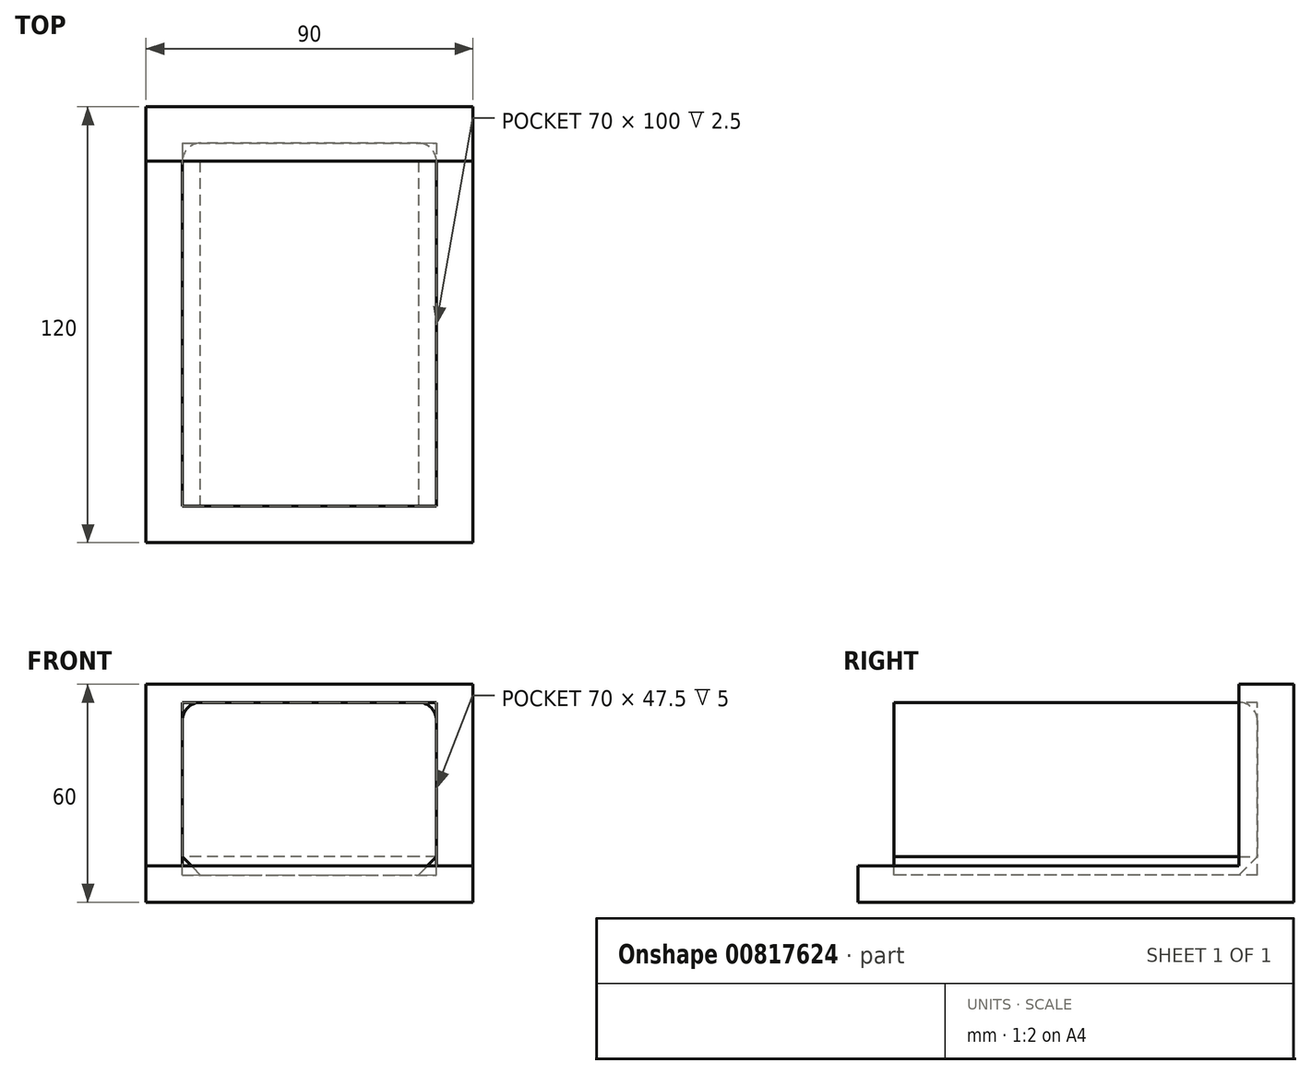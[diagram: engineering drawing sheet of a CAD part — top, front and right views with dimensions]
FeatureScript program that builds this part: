
annotation { "Feature Type Name" : "Feature", "Feature Type Description" : "" }
export const myFeature = defineFeature(function(context is Context, id is Id, definition is map)
    precondition{}
    {
        {
            var Q0;
            Q0=qCreatedBy(makeId("Top.planeOp"),FACE);
            var sketch = newSketch(context, id + "F0", { "sketchPlane" : qUnion([Q0])});
            skLineSegment(sketch, "E0.bottom", {"start": v(0, 0) * mm, "end": v(90, 0) * mm});
            skLineSegment(sketch, "E0.top", {"start": v(0, 120) * mm, "end": v(90, 120) * mm});
            skLineSegment(sketch, "E0.left", {"start": v(0, 0) * mm, "end": v(0, 120) * mm});
            skLineSegment(sketch, "E0.right", {"start": v(90, 0) * mm, "end": v(90, 120) * mm});
            skSolve(sketch);
        }
        {
            var Q0;
            Q0=qSketchRegion(id+"F0",true);
            extrude(context, id + "F1", {"entities" : qUnion([Q0]), "depth" : 10 * mm, "offsetDistance" : 25 * mm});
        }
        {
            var Q0;
            Q0=makeQuery(id+"F1.opExtrude","CAP_FACE",FACE,{"disambiguationData":[OSD([sQuery(id+"F0.wireOp",EDGE,"E0.bottom"),sQuery(id+"F0.wireOp",EDGE,"E0.top"),sQuery(id+"F0.wireOp",EDGE,"E0.left"),sQuery(id+"F0.wireOp",EDGE,"E0.right")])],"isStart":false});
            var sketch = newSketch(context, id + "F2", { "sketchPlane" : qUnion([Q0])});
            skLineSegment(sketch, "E1", {"start": v(0, 105) * mm, "end": v(90, 105) * mm});
            skSolve(sketch);
        }
        {
            var Q0;
            {var subQ0=sQuery(id+"F2.wireOp",EDGE,"E1");Q0=makeQuery(id+"F2.imprint","IMPRINT",FACE,{"disambiguationData":[TD([[makeQuery(id+"F2.imprint","IMPRINT",EDGE,{"derivedFrom":subQ0}),1.0]])]});}
            extrude(context, id + "F3", {"entities" : qUnion([Q0]), "operationType" : NewBodyOperationType.ADD, "depth" : 50 * mm, "offsetDistance" : 25 * mm});
        }
        {
            var Q0;
            Q0=makeQuery(id+"F3.opExtrude","CAP_FACE",FACE,{"disambiguationData":[OSD([sQuery(id+"F0.wireOp",EDGE,"E0.top"),sQuery(id+"F0.wireOp",EDGE,"E0.left"),sQuery(id+"F0.wireOp",EDGE,"E0.right"),sQuery(id+"F2.wireOp",EDGE,"E1")])],"isStart":false});
            cPlane(context, id + "F4", {"entities" : qUnion([Q0]), "cplaneType" : CPlaneType.OFFSET, "offset" : 5 * mm, "oppositeDirection" : true, "width" : 150 * mm, "height" : 150 * mm});
        }
        {
            var Q0;
            Q0=qCreatedBy(id+"F4.planeOp",FACE);
            var sketch = newSketch(context, id + "F5", { "sketchPlane" : qUnion([Q0])});
            skLineSegment(sketch, "E2.bottom", {"start": v(10, 110) * mm, "end": v(80, 110) * mm});
            skLineSegment(sketch, "E2.top", {"start": v(10, 10) * mm, "end": v(80, 10) * mm});
            skLineSegment(sketch, "E2.left", {"start": v(10, 110) * mm, "end": v(10, 10) * mm});
            skLineSegment(sketch, "E2.right", {"start": v(80, 110) * mm, "end": v(80, 10) * mm});
            skSolve(sketch);
        }
        {
            var Q0;
            {var subQ0=sQuery(id+"F5.wireOp",EDGE,"E2.top");Q0=makeQuery(id+"F5.imprint","IMPRINT",FACE,{"disambiguationData":[TD([[makeQuery(id+"F5.imprint","IMPRINT",EDGE,{"derivedFrom":subQ0}),1.0]])]});}
            var Q1;
            {var subQ0=sQuery(id+"F5.wireOp",EDGE,"E2.bottom");Q1=makeQuery(id+"F5.imprint","IMPRINT",FACE,{"disambiguationData":[TD([[makeQuery(id+"F5.imprint","IMPRINT",EDGE,{"derivedFrom":subQ0}),-1.0]])]});}
            extrude(context, id + "F6", {"entities" : qUnion([Q0, Q1]), "operationType" : NewBodyOperationType.REMOVE, "oppositeDirection" : true, "depth" : 47.5 * mm, "offsetDistance" : 25 * mm});
        }
        {
            var Q0;
            Q0=makeQuery(id+"F6.boolean.opBoolean","COPY",FACE,{"derivedFrom":makeQuery(id+"F6.opExtrude","CAP_FACE",FACE,{"disambiguationData":[OSD([sQuery(id+"F5.wireOp",EDGE,"E2.bottom"),sQuery(id+"F5.wireOp",EDGE,"E2.top"),sQuery(id+"F5.wireOp",EDGE,"E2.left"),sQuery(id+"F5.wireOp",EDGE,"E2.right")])],"isStart":false})});
            var Q1;
            Q1=makeQuery(id+"F6.boolean.opBoolean","COPY",FACE,{"derivedFrom":makeQuery(id+"F6.opExtrude","CAP_FACE",FACE,{"disambiguationData":[OSD([sQuery(id+"F5.wireOp",EDGE,"E2.bottom"),sQuery(id+"F5.wireOp",EDGE,"E2.top"),sQuery(id+"F5.wireOp",EDGE,"E2.left"),sQuery(id+"F5.wireOp",EDGE,"E2.right")])],"isStart":true})});
            extrude(context, id + "F7", {"entities" : qUnion([Q0]), "endBound" : BoundingType.UP_TO_SURFACE, "depth" : 40.5 * mm, "endBoundEntityFace" : qUnion([Q1]), "offsetDistance" : 25 * mm});
        }
        {
            var Q0;
            Q0=makeQuery(id+"F7.opExtrude","CAP_EDGE",EDGE,{"disambiguationData":[OSD([sQuery(id+"F5.wireOp",EDGE,"E2.right")])],"isStart":false});
            var Q1;
            Q1=makeQuery(id+"F7.opExtrude","CAP_EDGE",EDGE,{"disambiguationData":[OSD([sQuery(id+"F5.wireOp",EDGE,"E2.left")])],"isStart":false});
            var Q2;
            Q2=makeQuery(id+"F7.opExtrude","SWEPT_EDGE",EDGE,{"disambiguationData":[OSD([sQuery(id+"F5.wireOp",EDGE,"E2.bottom"),sQuery(id+"F5.wireOp",EDGE,"E2.right")])]});
            var Q3;
            Q3=makeQuery(id+"F7.opExtrude","CAP_EDGE",EDGE,{"disambiguationData":[OSD([sQuery(id+"F5.wireOp",EDGE,"E2.bottom")])],"isStart":false});
            var Q4;
            Q4=makeQuery(id+"F7.opExtrude","SWEPT_EDGE",EDGE,{"disambiguationData":[OSD([sQuery(id+"F5.wireOp",EDGE,"E2.bottom"),sQuery(id+"F5.wireOp",EDGE,"E2.left")])]});
            fillet(context, id + "F8", {"entities" : qUnion([Q0, Q1, Q2, Q3, Q4]), "radius" : 5 * mm, "tangentPropagation" : true, "allowEdgeOverflow" : false});
        }
        {
            var Q0;
            Q0=makeQuery(id+"F7.opExtrude","CAP_EDGE",EDGE,{"disambiguationData":[OSD([sQuery(id+"F5.wireOp",EDGE,"E2.right")])],"isStart":true});
            var Q1;
            Q1=makeQuery(id+"F7.opExtrude","CAP_EDGE",EDGE,{"disambiguationData":[OSD([sQuery(id+"F5.wireOp",EDGE,"E2.left")])],"isStart":true});
            chamfer(context, id + "F9", {"entities" : qUnion([Q0, Q1]), "width" : 5 * mm, "tangentPropagation" : true});
        }
    });
